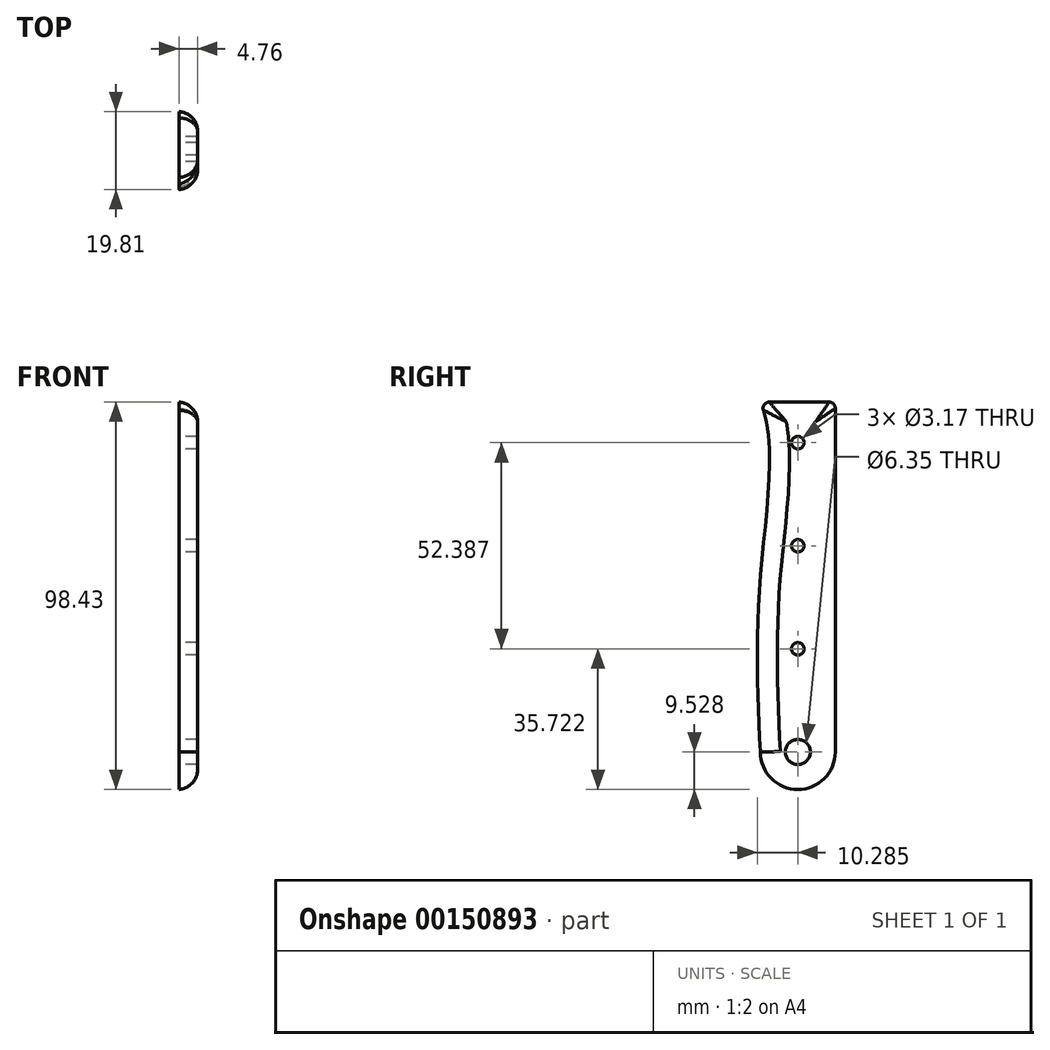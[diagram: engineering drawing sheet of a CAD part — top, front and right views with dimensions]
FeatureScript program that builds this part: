
annotation { "Feature Type Name" : "Feature", "Feature Type Description" : "" }
export const myFeature = defineFeature(function(context is Context, id is Id, definition is map)
    precondition{}
    {
        {
            var Q0;
            Q0=qCreatedBy(makeId("Right.planeOp"),FACE);
            var sketch = newSketch(context, id + "F0", { "sketchPlane" : qUnion([Q0])});
            skLineSegment(sketch, "E0", {"start": v(11.54, -116.33) * mm, "end": v(11.54, -2.03) * mm, "construction": true});
            skPoint(sketch, "E1", {"position": v(-7.5, -116.33) * mm});
            skPoint(sketch, "E2", {"position": v(2.02, -116.33) * mm});
            skPoint(sketch, "E3", {"position": v(2.02, -106.8) * mm});
            skLineSegment(sketch, "E4", {"start": v(-7.5, -106.8) * mm, "end": v(11.54, -106.8) * mm, "construction": true});
            skArc(sketch, "E5", {"start": v(-7.5, -106.8) * mm, "mid": v(2.02, -116.33) * mm, "end": v(11.54, -106.8) * mm});
            skLineSegment(sketch, "E6", {"start": v(11.54, -2.03) * mm, "end": v(11.54, -106.8) * mm, "construction": true});
            skPoint(sketch, "E7", {"position": v(-7.5, -17.9) * mm});
            skLineSegment(sketch, "E8", {"start": v(11.54, -2.03) * mm, "end": v(-26.56, -2.03) * mm});
            skLineSegment(sketch, "E9", {"start": v(2.02, -106.8) * mm, "end": v(2.02, -2.03) * mm, "construction": true});
            skPoint(sketch, "E10", {"position": v(-7.5, -62.35) * mm});
            skFitSpline(sketch, "E11", {"points": [v(-26.56, -2.03) * mm, v(-7.5, -17.9) * mm, v(-7.5, -62.35) * mm, v(-7.5, -106.8) * mm], "startDerivative": vector(86.2, -43.71) * mm, "endDerivative": vector(5.4, -117.19) * mm});
            skPoint(sketch, "E12", {"position": v(8.37, -2.03) * mm});
            skPoint(sketch, "E13", {"position": v(11.54, -17.9) * mm});
            skPoint(sketch, "E14", {"position": v(11.54, 13.85) * mm});
            skArc(sketch, "E15", {"start": v(11.54, 13.85) * mm, "mid": v(8.37, -2.03) * mm, "end": v(11.54, -17.9) * mm});
            skLineSegment(sketch, "E16", {"start": v(11.54, -17.9) * mm, "end": v(11.54, -106.8) * mm});
            skLineSegment(sketch, "E17", {"start": v(-26.56, 340.87) * mm, "end": v(11.54, 264.67) * mm});
            skPoint(sketch, "E18", {"position": v(11.54, 340.87) * mm});
            skLineSegment(sketch, "E19", {"start": v(11.54, 264.67) * mm, "end": v(11.54, 13.85) * mm});
            skLineSegment(sketch, "E20", {"start": v(-26.56, 340.87) * mm, "end": v(-26.56, -2.03) * mm});
            skPoint(sketch, "E21", {"position": v(2.02, -54.41) * mm});
            skPoint(sketch, "E22", {"position": v(2.02, -28.22) * mm});
            skPoint(sketch, "E23", {"position": v(2.02, -80.6) * mm});
            skPoint(sketch, "E24", {"position": v(-13.86, -2.03) * mm});
            skPoint(sketch, "E25", {"position": v(-13.86, -9.67) * mm});
            skLineSegment(sketch, "E26", {"start": v(-13.86, -9.67) * mm, "end": v(-13.86, 315.47) * mm});
            skLineSegment(sketch, "E27", {"start": v(-7.5, -17.9) * mm, "end": v(11.54, -17.9) * mm});
            skSolve(sketch);
        }
        {
            var Q0;
            {var subQ0=sQuery(id+"F0.wireOp",EDGE,"E5");Q0=makeQuery(id+"F0.imprint","IMPRINT",FACE,{"disambiguationData":[TD([[makeQuery(id+"F0.imprint","IMPRINT",EDGE,{"derivedFrom":subQ0}),1.0]])]});}
            extrude(context, id + "F4", {"entities" : qUnion([Q0]), "depth" : 4.76 * mm});
        }
        {
            var Q0;
            Q0=sQuery(id+"F0.wireOp",VERTEX,"E22");
            var Q1;
            Q1=sQuery(id+"F0.wireOp",VERTEX,"E21");
            var Q2;
            Q2=sQuery(id+"F0.wireOp",VERTEX,"E23");
            var Q3;
            Q3=makeQuery(id+"F4.opExtrude","SWEPT_BODY",BODY,{"disambiguationData":[OSD([sQuery(id+"F0.wireOp",EDGE,"E5"),sQuery(id+"F0.wireOp",EDGE,"E11"),sQuery(id+"F0.wireOp",EDGE,"E16"),sQuery(id+"F0.wireOp",EDGE,"E27")])]});
            hole(context, id + "F5", {"style" : HoleStyle.SIMPLE, "endStyle" : HoleEndStyle.THROUGH, "oppositeDirection" : true, "holeDiameter" : 3.17 * mm, "locations" : qUnion([Q0, Q1, Q2]), "scope" : qUnion([Q3]), "isTappedThrough" : true});
        }
        {
            var Q0;
            Q0=sQuery(id+"F0.wireOp",VERTEX,"E3");
            var Q1;
            Q1=makeQuery(id+"F4.opExtrude","SWEPT_BODY",BODY,{"disambiguationData":[OSD([sQuery(id+"F0.wireOp",EDGE,"E5"),sQuery(id+"F0.wireOp",EDGE,"E11"),sQuery(id+"F0.wireOp",EDGE,"E16"),sQuery(id+"F0.wireOp",EDGE,"E27")])]});
            hole(context, id + "F1", {"style" : HoleStyle.SIMPLE, "endStyle" : HoleEndStyle.THROUGH, "oppositeDirection" : true, "holeDiameter" : 6.35 * mm, "locations" : qUnion([Q0]), "scope" : qUnion([Q1]), "isTappedThrough" : true});
        }
        {
            var Q0;
            Q0=makeQuery(id+"F4.opExtrude","SWEPT_EDGE",EDGE,{"disambiguationData":[OSD([sQuery(id+"F0.wireOp",EDGE,"E11"),sQuery(id+"F0.wireOp",EDGE,"E27")])]});
            var Q1;
            Q1=makeQuery(id+"F4.opExtrude","SWEPT_EDGE",EDGE,{"disambiguationData":[OSD([sQuery(id+"F0.wireOp",EDGE,"E15"),sQuery(id+"F0.wireOp",EDGE,"E16"),sQuery(id+"F0.wireOp",EDGE,"E27")])]});
            fillet(context, id + "F2", {"entities" : qUnion([Q0, Q1]), "radius" : 1.59 * mm, "tangentPropagation" : true, "allowEdgeOverflow" : false});
        }
        {
            var Q0;
            Q0=makeQuery(id+"F4.opExtrude","CAP_EDGE",EDGE,{"disambiguationData":[OSD([sQuery(id+"F0.wireOp",EDGE,"E16")])],"isStart":false});
            var Q1;
            Q1=makeQuery(id+"F4.opExtrude","CAP_EDGE",EDGE,{"disambiguationData":[OSD([sQuery(id+"F0.wireOp",EDGE,"E11")])],"isStart":false});
            var Q2;
            Q2=makeQuery(id+"F4.opExtrude","CAP_EDGE",EDGE,{"disambiguationData":[OSD([sQuery(id+"F0.wireOp",EDGE,"E5")])],"isStart":false});
            var Q3;
            Q3=makeQuery(id+"F4.opExtrude","CAP_EDGE",EDGE,{"disambiguationData":[OSD([sQuery(id+"F0.wireOp",EDGE,"E27")])],"isStart":false});
            fillet(context, id + "F3", {"entities" : qUnion([Q0, Q1, Q2, Q3]), "radius" : 5.08 * mm, "tangentPropagation" : true, "allowEdgeOverflow" : false});
        }
    });
